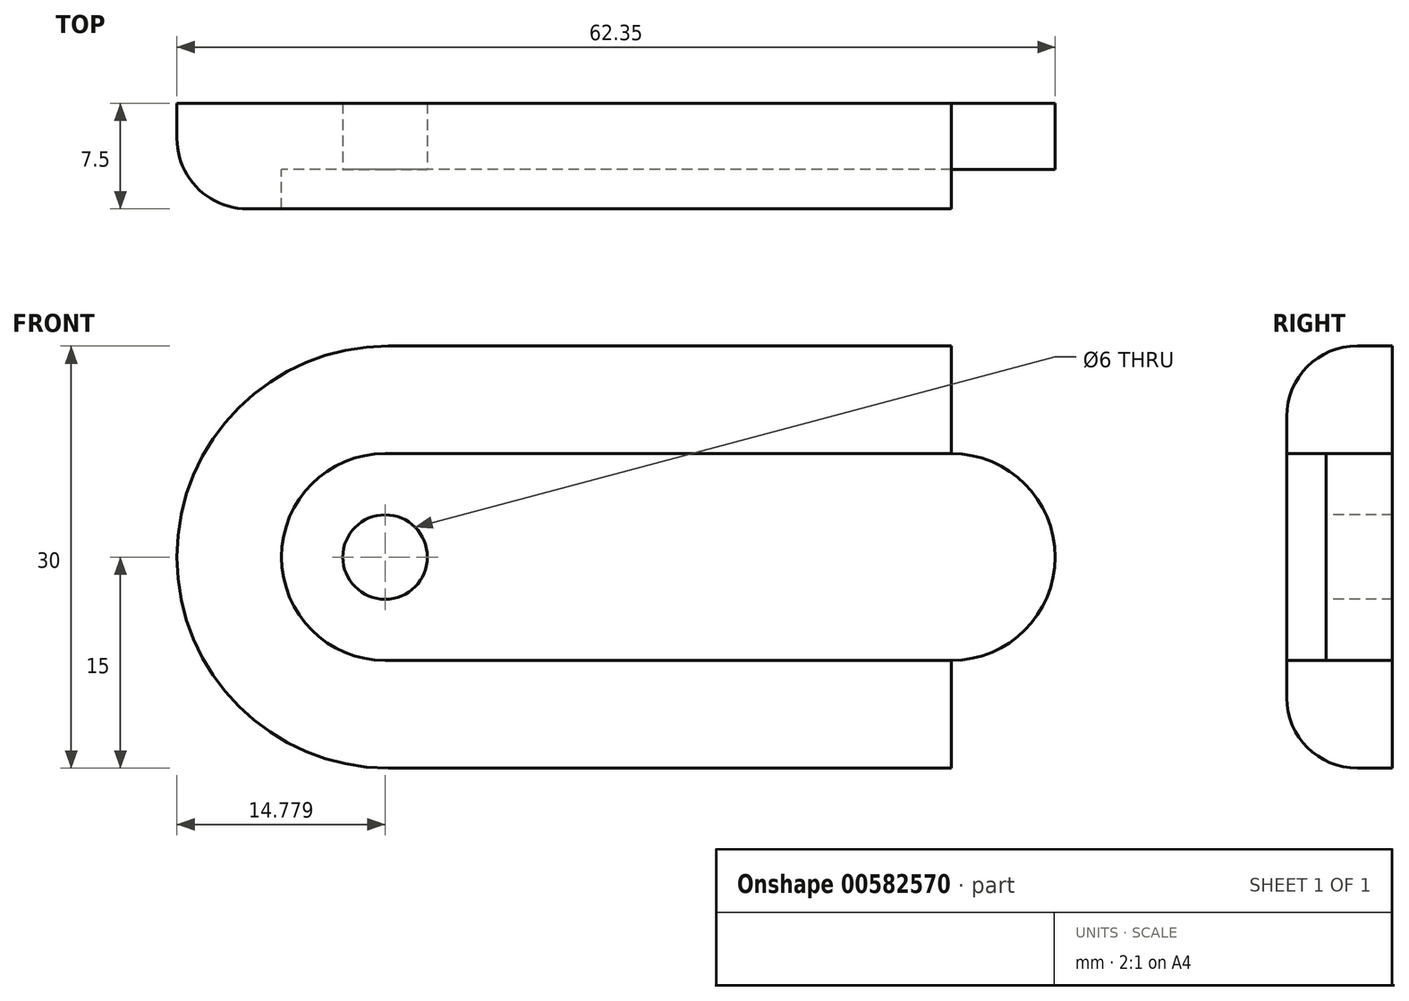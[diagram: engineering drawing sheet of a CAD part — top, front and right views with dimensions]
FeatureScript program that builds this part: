
annotation { "Feature Type Name" : "Feature", "Feature Type Description" : "" }
export const myFeature = defineFeature(function(context is Context, id is Id, definition is map)
    precondition{}
    {
        {
            var Q0;
            Q0=qCreatedBy(makeId("Front.planeOp"),FACE);
            var sketch = newSketch(context, id + "F0", { "sketchPlane" : qUnion([Q0])});
            skCircle(sketch, "E0", {"center": v(0, 0) * mm, "radius": 7.35 * mm});
            skCircle(sketch, "E1", {"center": v(-40.22, 0) * mm, "radius": 7.35 * mm});
            skLineSegment(sketch, "E2", {"start": v(0, 7.35) * mm, "end": v(-40.22, 7.35) * mm});
            skLineSegment(sketch, "E3", {"start": v(-40.22, -7.35) * mm, "end": v(0, -7.35) * mm});
            skLineSegment(sketch, "E4", {"start": v(0, 0) * mm, "end": v(0, 15) * mm});
            skLineSegment(sketch, "E5", {"start": v(0, 15) * mm, "end": v(-40, 15) * mm});
            skLineSegment(sketch, "E6", {"start": v(-40, -15) * mm, "end": v(0, -15) * mm});
            skLineSegment(sketch, "E7", {"start": v(0, -15) * mm, "end": v(0, 0) * mm});
            skArc(sketch, "E8", {"start": v(-40, 15) * mm, "mid": v(-55, 0) * mm, "end": v(-40, -15) * mm});
            skSolve(sketch);
        }
        {
            var Q0;
            {var subQ1=sQuery(id+"F0.wireOp",EDGE,"E2");Q0=makeQuery(id+"F0.imprint","IMPRINT",FACE,{"disambiguationData":[TD([[makeQuery(id+"F0.imprint","IMPRINT",EDGE,{"derivedFrom":subQ1}),-1.0]])]});}
            extrude(context, id + "F1", {"entities" : qUnion([Q0]), "depth" : 7.5 * mm, "offsetDistance" : 25 * mm});
        }
        {
            var Q0;
            {var subQ0=sQuery(id+"F0.wireOp",EDGE,"E2");Q0=makeQuery(id+"F0.imprint","IMPRINT",FACE,{"disambiguationData":[TD([[makeQuery(id+"F0.imprint","IMPRINT",EDGE,{"derivedFrom":subQ0}),1.0]])]});}
            var Q1;
            {var subQ0=sQuery(id+"F0.wireOp",EDGE,"E1");var subQ1=makeQuery(id+"F0.imprint","INTERSECT",VERTEX,{"derivedFrom":[subQ0,sQuery(id+"F0.wireOp",EDGE,"E2")]});Q1=makeQuery(id+"F0.imprint","IMPRINT",FACE,{"disambiguationData":[TD([[makeQuery(id+"F0.imprint","IMPRINT",EDGE,{"disambiguationData":[TD([[subQ1,-1.0]])],"derivedFrom":subQ0}),1.0]])]});}
            var Q2;
            {var subQ0=sQuery(id+"F0.wireOp",EDGE,"E4");var subQ3=sQuery(id+"F0.wireOp",EDGE,"E7");var subQ5=makeQuery(id+"F0.imprint","INTERSECT",VERTEX,{"derivedFrom":[subQ0,subQ3]});Q2=makeQuery(id+"F0.imprint","IMPRINT",FACE,{"disambiguationData":[TD([[makeQuery(id+"F0.imprint","IMPRINT",EDGE,{"disambiguationData":[TD([[subQ5,-1.0]])],"derivedFrom":subQ0}),-1.0]])]});}
            var Q3;
            {var subQ0=sQuery(id+"F0.wireOp",EDGE,"E4");var subQ3=sQuery(id+"F0.wireOp",EDGE,"E7");var subQ5=makeQuery(id+"F0.imprint","INTERSECT",VERTEX,{"derivedFrom":[subQ0,subQ3]});Q3=makeQuery(id+"F0.imprint","IMPRINT",FACE,{"disambiguationData":[TD([[makeQuery(id+"F0.imprint","IMPRINT",EDGE,{"disambiguationData":[TD([[subQ5,-1.0]])],"derivedFrom":subQ0}),1.0]])]});}
            extrude(context, id + "F2", {"entities" : qUnion([Q0, Q1, Q2, Q3]), "operationType" : NewBodyOperationType.ADD, "depth" : 4.7 * mm, "offsetDistance" : 25 * mm});
        }
        {
            var Q0;
            Q0=makeQuery(id+"F1.opExtrude","CAP_EDGE",EDGE,{"disambiguationData":[OSD([sQuery(id+"F0.wireOp",EDGE,"E5")])],"isStart":false});
            fillet(context, id + "F3", {"entities" : qUnion([Q0]), "radius" : 5 * mm, "tangentPropagation" : true, "allowEdgeOverflow" : false});
        }
        {
            var Q0;
            Q0=makeQuery(id+"F2.opExtrude","CAP_FACE",FACE,{"disambiguationData":[OSD([sQuery(id+"F0.wireOp",EDGE,"E0"),sQuery(id+"F0.wireOp",EDGE,"E1"),sQuery(id+"F0.wireOp",EDGE,"E2"),sQuery(id+"F0.wireOp",EDGE,"E3")])],"isStart":false});
            var sketch = newSketch(context, id + "F4", { "sketchPlane" : qUnion([Q0])});
            skCircle(sketch, "E9", {"center": v(-40.22, 0) * mm, "radius": 3 * mm});
            skSolve(sketch);
        }
        {
            var Q0;
            Q0 = qSketchRegion(id + "F4", true);
            extrude(context, id + "F5", {"entities" : qUnion([Q0]), "operationType" : NewBodyOperationType.REMOVE, "oppositeDirection" : true, "depth" : 25 * mm, "offsetDistance" : 25 * mm});
        }
    });
